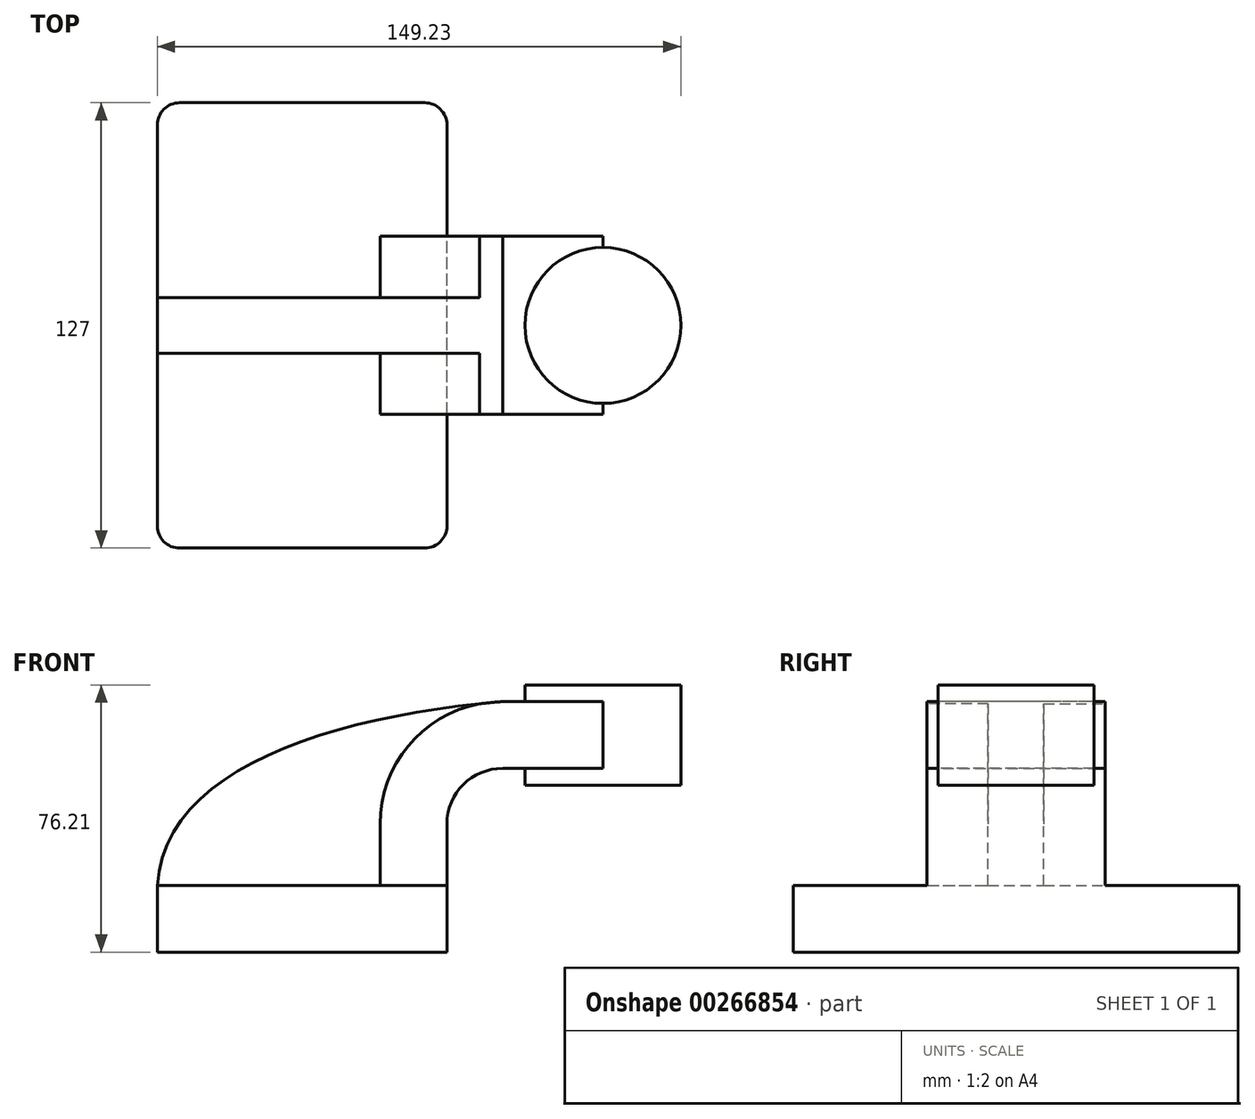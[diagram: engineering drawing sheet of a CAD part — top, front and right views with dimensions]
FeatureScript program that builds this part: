
annotation { "Feature Type Name" : "Feature", "Feature Type Description" : "" }
export const myFeature = defineFeature(function(context is Context, id is Id, definition is map)
    precondition{}
    {
        {
            var Q0;
            Q0=qCreatedBy(makeId("Front.planeOp"),FACE);
            var sketch = newSketch(context, id + "F0", { "sketchPlane" : qUnion([Q0])});
            skLineSegment(sketch, "E0.bottom", {"start": v(41.27, 9.53) * mm, "end": v(-41.28, 9.53) * mm});
            skLineSegment(sketch, "E0.top", {"start": v(41.28, -9.52) * mm, "end": v(-41.27, -9.52) * mm});
            skLineSegment(sketch, "E0.left", {"start": v(41.28, 9.53) * mm, "end": v(41.28, -9.52) * mm});
            skLineSegment(sketch, "E0.right", {"start": v(-41.28, 9.53) * mm, "end": v(-41.27, -9.52) * mm});
            skPoint(sketch, "E0.middle", {"position": v(0, 0) * mm});
            skLineSegment(sketch, "E1.bottom", {"start": v(107.95, 38.1) * mm, "end": v(57.15, 38.1) * mm});
            skLineSegment(sketch, "E1.top", {"start": v(107.95, 66.68) * mm, "end": v(57.15, 66.68) * mm});
            skLineSegment(sketch, "E1.left", {"start": v(107.95, 38.1) * mm, "end": v(107.95, 66.68) * mm});
            skLineSegment(sketch, "E1.right", {"start": v(57.15, 38.1) * mm, "end": v(57.15, 66.68) * mm});
            skPoint(sketch, "E1.middle", {"position": v(82.55, 52.39) * mm});
            skLineSegment(sketch, "E2", {"start": v(41.27, 9.53) * mm, "end": v(41.27, 27) * mm});
            skArc(sketch, "E3", {"start": v(41.27, 27) * mm, "mid": v(45.92, 38.23) * mm, "end": v(57.15, 42.88) * mm});
            skLineSegment(sketch, "E4", {"start": v(57.15, 42.88) * mm, "end": v(85.72, 42.88) * mm});
            skLineSegment(sketch, "E5.0", {"start": v(57.15, 61.93) * mm, "end": v(85.72, 61.93) * mm});
            skArc(sketch, "E5.1", {"start": v(22.23, 27) * mm, "mid": v(32.45, 51.7) * mm, "end": v(57.15, 61.93) * mm});
            skLineSegment(sketch, "E5.2", {"start": v(22.22, 9.53) * mm, "end": v(22.22, 27) * mm});
            skLineSegment(sketch, "E6", {"start": v(85.72, 38.1) * mm, "end": v(85.72, 66.68) * mm});
            skFitSpline(sketch, "E7", {"points": [v(-41.28, 9.53) * mm, v(57.15, 61.93) * mm], "startDerivative": vector(6.2, 100.42) * mm, "endDerivative": vector(146.16, 12.51) * mm});
            skSolve(sketch);
        }
        {
            var Q0;
            Q0=makeQuery(id+"F0.imprint","IMPRINT",FACE,{"disambiguationData":[TD([[makeQuery(id+"F0.imprint","IMPRINT",EDGE,{"derivedFrom":sQuery(id+"F0.wireOp",EDGE,"E0.top")}),-1.0]])]});
            extrude(context, id + "F1", {"entities" : qUnion([Q0]), "endBound" : BoundingType.SYMMETRIC, "depth" : 127 * mm});
        }
        {
            var Q0;
            {var subQ1=sQuery(id+"F0.wireOp",EDGE,"E2");Q0=makeQuery(id+"F0.imprint","IMPRINT",FACE,{"disambiguationData":[TD([[makeQuery(id+"F0.imprint","IMPRINT",EDGE,{"derivedFrom":subQ1}),1.0]])]});}
            var Q1;
            {var subQ0=sQuery(id+"F0.wireOp",EDGE,"E4");Q1=makeQuery(id+"F0.imprint","IMPRINT",FACE,{"disambiguationData":[TD([[makeQuery(id+"F0.imprint","IMPRINT",EDGE,{"derivedFrom":subQ0}),1.0]])]});}
            extrude(context, id + "F2", {"entities" : qUnion([Q0, Q1]), "operationType" : NewBodyOperationType.ADD, "endBound" : BoundingType.SYMMETRIC, "depth" : 50.8 * mm});
        }
        {
            var Q0;
            {var subQ0=sQuery(id+"F0.wireOp",EDGE,"E7");var subQ1=sQuery(id+"F0.wireOp",EDGE,"E5.1");var subQ3=makeQuery(id+"F0.imprint","INTERSECT",VERTEX,{"derivedFrom":[subQ1,subQ0]});Q0=makeQuery(id+"F0.imprint","IMPRINT",FACE,{"disambiguationData":[TD([[makeQuery(id+"F0.imprint","IMPRINT",EDGE,{"disambiguationData":[TD([[subQ3,-1.0]])],"derivedFrom":subQ1}),-1.0]])]});}
            var Q1;
            Q1=makeQuery(id+"F0.imprint","IMPRINT",FACE,{"disambiguationData":[TD([[makeQuery(id+"F0.imprint","IMPRINT",EDGE,{"derivedFrom":sQuery(id+"F0.wireOp",EDGE,"E0.top")}),-1.0]])]});
            var Q2;
            {var subQ3=sQuery(id+"F0.wireOp",EDGE,"E5.2");Q2=makeQuery(id+"F0.imprint","IMPRINT",FACE,{"disambiguationData":[TD([[makeQuery(id+"F0.imprint","IMPRINT",EDGE,{"derivedFrom":subQ3}),1.0]])]});}
            extrude(context, id + "F3", {"entities" : qUnion([Q0, Q1, Q2]), "operationType" : NewBodyOperationType.ADD, "endBound" : BoundingType.SYMMETRIC, "depth" : 15.88 * mm});
        }
        {
            var Q0;
            {var subQ0=sQuery(id+"F0.wireOp",EDGE,"E1.left");Q0=makeQuery(id+"F0.imprint","IMPRINT",FACE,{"disambiguationData":[TD([[makeQuery(id+"F0.imprint","IMPRINT",EDGE,{"derivedFrom":subQ0}),1.0]])]});}
            var Q1;
            Q1=sQuery(id+"F0.wireOp",EDGE,"E6");
            revolve(context, id + "F4", {"operationType" : NewBodyOperationType.ADD, "entities" : qUnion([Q0]), "axis" : qUnion([Q1]), "revolveType" : RevolveType.FULL});
        }
        {
            var Q0;
            Q0=makeQuery(id+"F1.opExtrude","CAP_EDGE",EDGE,{"disambiguationData":[OSD([sQuery(id+"F0.wireOp",EDGE,"E0.right")])],"isStart":true});
            var Q1;
            Q1=makeQuery(id+"F1.opExtrude","CAP_EDGE",EDGE,{"disambiguationData":[OSD([sQuery(id+"F0.wireOp",EDGE,"E0.left")])],"isStart":true});
            var Q2;
            Q2=makeQuery(id+"F1.opExtrude","CAP_EDGE",EDGE,{"disambiguationData":[OSD([sQuery(id+"F0.wireOp",EDGE,"E0.right")])],"isStart":false});
            var Q3;
            Q3=makeQuery(id+"F1.opExtrude","CAP_EDGE",EDGE,{"disambiguationData":[OSD([sQuery(id+"F0.wireOp",EDGE,"E0.left")])],"isStart":false});
            fillet(context, id + "F5", {"entities" : qUnion([Q0, Q1, Q2, Q3]), "radius" : 6.35 * mm, "tangentPropagation" : true, "allowEdgeOverflow" : false});
        }
    });
